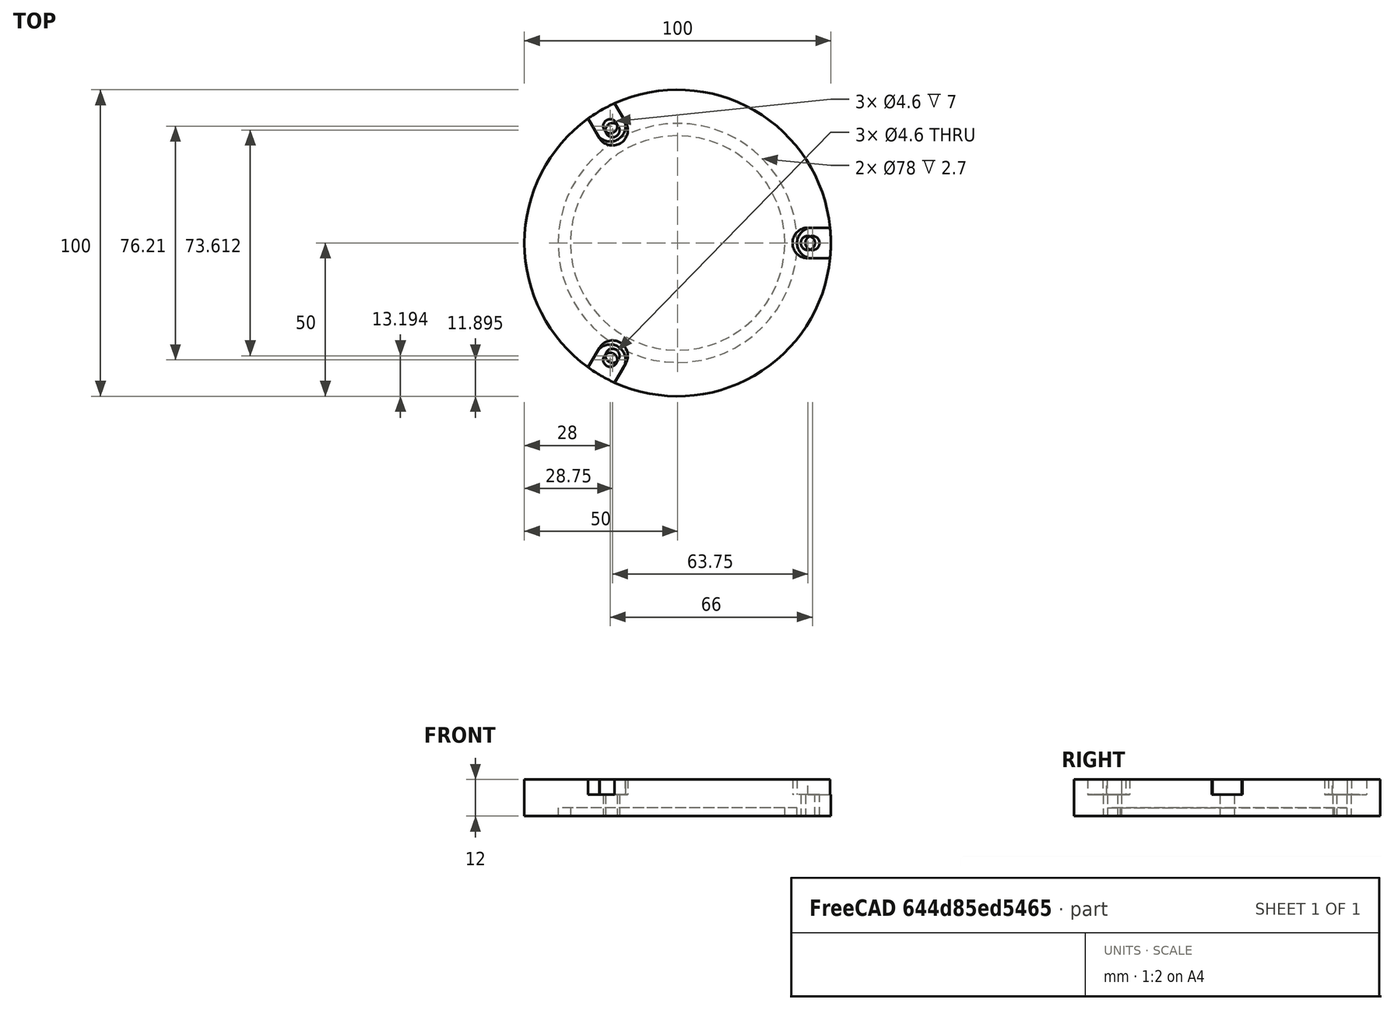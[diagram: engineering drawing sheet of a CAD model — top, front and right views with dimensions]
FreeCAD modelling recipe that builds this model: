
FCSTD DOCUMENT  (FreeCAD 0.20R29603 (Git))
Label: PhilippsXL30_Blindflange_100
License: All rights reserved
LicenseURL: http://en.wikipedia.org/wiki/All_rights_reserved
objects: TechDraw::DrawViewDimension×18, Part::Cylinder×9, Part::MultiFuse×4, TechDraw::DrawProjGroupItem×4, Part::Box×3, Part::Cut×2, Part::Feature×2, TechDraw::DrawSVGTemplate×2, TechDraw::DrawProjGroup×2, TechDraw::DrawPage×2, Part::Compound×1, TechDraw::DrawViewSection×1
note: 21 computed .brp shape members not serialized (recipe doc carries the construction recipe); baked Part::Feature solids carry a one-line shape summary decoded from their .brp

FEATURE [Part::Cylinder] Cylinder  label="Zylinder"
  Angle = 360
  AttacherType = Attacher::AttachEngine3D
  FirstAngle = 0
  Height = 12
  Radius = 50
  SecondAngle = 0
FEATURE [Part::Cylinder] Cylinder001  label="Zylinder001"
  Angle = 360
  AttacherType = Attacher::AttachEngine3D
  FirstAngle = 0
  Height = 2.7
  Radius = 39
  SecondAngle = 0
FEATURE [Part::Cut] Cut
  Base = -> Cylinder
  Tool = -> Cylinder001
FEATURE [Part::Cylinder] Cylinder002  label="Zylinder002"
  Angle = 360
  AttacherType = Attacher::AttachEngine3D
  FirstAngle = 0
  Height = 2.7
  Radius = 35
  SecondAngle = 0
FEATURE [Part::MultiFuse] Fusion
  Shapes = -> [Cylinder002,Cut]
FEATURE [Part::Cylinder] Cylinder003  label="Zylinder003"
  Angle = 360
  AttacherType = Attacher::AttachEngine3D
  FirstAngle = 0
  Height = 12
  Placement = pos=(44,0,0) rot=(0,0,1;0rad)
  Radius = 2.3
  SecondAngle = 0
FEATURE [Part::Cylinder] Cylinder004  label="Zylinder004"
  Angle = 360
  AttacherType = Attacher::AttachEngine3D
  FirstAngle = 0
  Height = 5
  Placement = pos=(44,0,7) rot=(0,0,1;0rad)
  Radius = 5
  SecondAngle = 0
FEATURE [Part::Box] Box  label="Würfel"
  AttacherType = Attacher::AttachEngine3D
  Height = 5
  Length = 10
  Placement = pos=(42.5,-5,7) rot=(0,0,1;0rad)
  Width = 10
FEATURE [Part::MultiFuse] Fusion001
  Shapes = -> [Box,Cylinder003,Cylinder004]
FEATURE [Part::Box] Box001  label="Würfel001"
  AttacherType = Attacher::AttachEngine3D
  Height = 5
  Length = 10
  Placement = pos=(42.5,-5,7) rot=(0,0,1;0rad)
  Width = 10
FEATURE [Part::Cylinder] Cylinder005  label="Zylinder005"
  Angle = 360
  AttacherType = Attacher::AttachEngine3D
  FirstAngle = 0
  Height = 12
  Placement = pos=(44,0,0) rot=(0,0,1;0rad)
  Radius = 2.3
  SecondAngle = 0
FEATURE [Part::Cylinder] Cylinder006  label="Zylinder006"
  Angle = 360
  AttacherType = Attacher::AttachEngine3D
  FirstAngle = 0
  Height = 5
  Placement = pos=(44,0,7) rot=(0,0,1;0rad)
  Radius = 5
  SecondAngle = 0
FEATURE [Part::MultiFuse] Fusion002
  Placement = pos=(0,0,0) rot=(0,0,1;2.0944rad)
  Shapes = -> [Box001,Cylinder005,Cylinder006]
FEATURE [Part::Box] Box002  label="Würfel002"
  AttacherType = Attacher::AttachEngine3D
  Height = 5
  Length = 10
  Placement = pos=(42.5,-5,7) rot=(0,0,1;0rad)
  Width = 10
FEATURE [Part::Cylinder] Cylinder007  label="Zylinder007"
  Angle = 360
  AttacherType = Attacher::AttachEngine3D
  FirstAngle = 0
  Height = 12
  Placement = pos=(44,0,0) rot=(0,0,1;0rad)
  Radius = 2.3
  SecondAngle = 0
FEATURE [Part::Cylinder] Cylinder008  label="Zylinder008"
  Angle = 360
  AttacherType = Attacher::AttachEngine3D
  FirstAngle = 0
  Height = 5
  Placement = pos=(44,0,7) rot=(0,0,1;0rad)
  Radius = 5
  SecondAngle = 0
FEATURE [Part::MultiFuse] Fusion003
  Placement = pos=(0,0,0) rot=(0,0,1;4.18879rad)
  Shapes = -> [Box002,Cylinder007,Cylinder008]
FEATURE [Part::Compound] Compound
  Links = -> [Fusion001,Fusion002,Fusion003]
FEATURE [Part::Cut] Cut001
  Base = -> Fusion
  Tool = -> Compound
FEATURE [Part::Feature] Cut001_solid  label="Cut001 (Solid)"
  shape: bbox 100 x 100 x 12 mm, 28 faces (baked)
FEATURE [TechDraw::DrawSVGTemplate] Template
  EditableTexts = Designed_by_Name=Thomas Spielauer; FC-Date=2023-07-05; FC-SC=mm; FC-SH=01/02; FC-Title=Philipps XL 30 blind flange (100); Subtitle=Compatible
  Height = 210
  Orientation = 1
  Width = 297
FEATURE [TechDraw::DrawProjGroupItem] ProjItem  label="Front"
  CoarseView = false
  Direction = (0,0,1)
  Focus = 100
  HardHidden = false
  IsoCount = 0
  IsoHidden = false
  IsoVisible = false
  LockPosition = true
  Perspective = false
  Rotation = 0
  RotationVector = (-1,0,0)
  ScaleType = 2
  SeamHidden = false
  SeamVisible = true
  SmoothHidden = false
  SmoothVisible = true
  Source = -> [Cut001]
  Type = 0
  X = 0
  XDirection = (-1,0,0)
  Y = 0
FEATURE [TechDraw::DrawProjGroupItem] ProjItem001  label="Right"
  CoarseView = false
  Direction = (-1,0,1e-16)
  Focus = 100
  HardHidden = false
  IsoCount = 0
  IsoHidden = false
  IsoVisible = false
  LockPosition = false
  Perspective = false
  Rotation = 0
  RotationVector = (1,0,0)
  ScaleType = 2
  SeamHidden = false
  SeamVisible = true
  SmoothHidden = false
  SmoothVisible = true
  Source = -> [Cut001]
  Type = 2
  X = -115
  XDirection = (-1e-16,0,-1)
  Y = 0
FEATURE [TechDraw::DrawViewDimension] Dimension
  AngleOverride = false
  Arbitrary = false
  ArbitraryTolerances = false
  EqualTolerance = true
  ExtensionAngle = 0
  FormatSpec = %.2w
  FormatSpecOverTolerance = %+.2w
  FormatSpecUnderTolerance = %+.2w
  Inverted = false
  LineAngle = 0
  LockPosition = false
  MeasureType = 1
  OverTolerance = 0
  References2D = -> [ProjItem001]
  Rotation = 0
  ScaleType = 0
  TheoreticalExact = false
  Type = 0
  UnderTolerance = 0
  X = 19.2083
  Y = 59.9207
FEATURE [TechDraw::DrawViewDimension] Dimension001
  AngleOverride = false
  Arbitrary = false
  ArbitraryTolerances = false
  EqualTolerance = true
  ExtensionAngle = 0
  FormatSpec = %.2w
  FormatSpecOverTolerance = %+.2w
  FormatSpecUnderTolerance = %+.2w
  Inverted = false
  LineAngle = 0
  LockPosition = false
  MeasureType = 1
  OverTolerance = 0
  References2D = -> [ProjItem001]
  Rotation = 0
  ScaleType = 0
  TheoreticalExact = false
  Type = 0
  UnderTolerance = 0
  X = -19.7857
  Y = -35.9202
FEATURE [TechDraw::DrawViewDimension] Dimension002
  AngleOverride = false
  Arbitrary = false
  ArbitraryTolerances = false
  EqualTolerance = true
  ExtensionAngle = 0
  FormatSpec = %.2w
  FormatSpecOverTolerance = %+.2w
  FormatSpecUnderTolerance = %+.2w
  Inverted = false
  LineAngle = 0
  LockPosition = false
  MeasureType = 1
  OverTolerance = 0
  References2D = -> [ProjItem001]
  Rotation = 0
  ScaleType = 0
  TheoreticalExact = false
  Type = 0
  UnderTolerance = 0
  X = -13.2618
  Y = 53.2317
FEATURE [TechDraw::DrawViewDimension] Dimension003
  AngleOverride = false
  Arbitrary = false
  ArbitraryTolerances = false
  EqualTolerance = true
  ExtensionAngle = 0
  FormatSpec = %.2w
  FormatSpecOverTolerance = %+.2w
  FormatSpecUnderTolerance = %+.2w
  Inverted = false
  LineAngle = 0
  LockPosition = false
  MeasureType = 1
  OverTolerance = 0
  References2D = -> [ProjItem001]
  Rotation = 0
  ScaleType = 0
  TheoreticalExact = false
  Type = 0
  UnderTolerance = 0
  X = 0.218931
  Y = -64.4994
FEATURE [TechDraw::DrawViewDimension] Dimension004
  AngleOverride = false
  Arbitrary = false
  ArbitraryTolerances = false
  EqualTolerance = true
  ExtensionAngle = 0
  FormatSpec = R%.2w
  FormatSpecOverTolerance = %+.2w
  FormatSpecUnderTolerance = %+.2w
  Inverted = false
  LineAngle = 0
  LockPosition = false
  MeasureType = 1
  OverTolerance = 0
  References2D = -> [ProjItem]
  Rotation = 0
  ScaleType = 0
  TheoreticalExact = false
  Type = 4
  UnderTolerance = 0
  X = -6.18987
  Y = 19.3502
FEATURE [TechDraw::DrawViewDimension] Dimension005
  AngleOverride = false
  Arbitrary = false
  ArbitraryTolerances = false
  EqualTolerance = true
  ExtensionAngle = 0
  FormatSpec = ⌀%.2w (3x)
  FormatSpecOverTolerance = %+.2w
  FormatSpecUnderTolerance = %+.2w
  Inverted = false
  LineAngle = 0
  LockPosition = false
  MeasureType = 1
  OverTolerance = 0
  References2D = -> [ProjItem]
  Rotation = 0
  ScaleType = 0
  TheoreticalExact = false
  Type = 5
  UnderTolerance = 0
  X = -25.1053
  Y = -2.37354
FEATURE [TechDraw::DrawViewDimension] Dimension006
  AngleOverride = false
  Arbitrary = false
  ArbitraryTolerances = false
  EqualTolerance = true
  ExtensionAngle = 0
  FormatSpec = ⌀%.2w (3x)
  FormatSpecOverTolerance = %+.2w
  FormatSpecUnderTolerance = %+.2w
  Inverted = false
  LineAngle = 0
  LockPosition = false
  MeasureType = 1
  OverTolerance = 0
  References2D = -> [ProjItem]
  Rotation = 0
  ScaleType = 0
  TheoreticalExact = false
  Type = 5
  UnderTolerance = 0
  X = 28.0562
  Y = -19.9323
FEATURE [TechDraw::DrawProjGroupItem] ProjItem002  label="Rear"
  CoarseView = false
  Direction = (0,0,-1)
  Focus = 100
  HardHidden = false
  IsoCount = 0
  IsoHidden = false
  IsoVisible = false
  LockPosition = false
  Perspective = false
  Rotation = 0
  RotationVector = (1,0,0)
  ScaleType = 2
  SeamHidden = false
  SeamVisible = true
  SmoothHidden = false
  SmoothVisible = true
  Source = -> [Cut001]
  Type = 3
  X = 115
  XDirection = (1,0,0)
  Y = 0
FEATURE [TechDraw::DrawProjGroup] ProjGroup
  Anchor = -> ProjItem
  AutoDistribute = true
  LockPosition = false
  ProjectionType = 0
  Rotation = 0
  ScaleType = 0
  Source = -> [Cut001]
  Views = -> [ProjItem,ProjItem001,ProjItem002]
  X = 116.126
  Y = 130.742
  spacingX = 15
  spacingY = 15
FEATURE [TechDraw::DrawViewDimension] Dimension007
  AngleOverride = false
  Arbitrary = false
  ArbitraryTolerances = false
  EqualTolerance = true
  ExtensionAngle = 0
  FormatSpec = ⌀%.2w
  FormatSpecOverTolerance = %+.2w
  FormatSpecUnderTolerance = %+.2w
  Inverted = false
  LineAngle = 0
  LockPosition = false
  MeasureType = 1
  OverTolerance = 0
  References2D = -> [ProjItem002]
  Rotation = 0
  ScaleType = 0
  TheoreticalExact = false
  Type = 5
  UnderTolerance = 0
  X = 42.307
  Y = -41.3708
FEATURE [TechDraw::DrawViewDimension] Dimension008
  AngleOverride = false
  Arbitrary = false
  ArbitraryTolerances = false
  EqualTolerance = true
  ExtensionAngle = 0
  FormatSpec = ⌀%.2w
  FormatSpecOverTolerance = %+.2w
  FormatSpecUnderTolerance = %+.2w
  Inverted = false
  LineAngle = 0
  LockPosition = false
  MeasureType = 1
  OverTolerance = 0
  References2D = -> [ProjItem002]
  Rotation = 0
  ScaleType = 0
  TheoreticalExact = false
  Type = 5
  UnderTolerance = 0
  X = 34.8456
  Y = -46.8908
FEATURE [TechDraw::DrawViewDimension] Dimension009
  AngleOverride = false
  Arbitrary = false
  ArbitraryTolerances = false
  EqualTolerance = true
  ExtensionAngle = 0
  FormatSpec = ⌀%.2w
  FormatSpecOverTolerance = %+.2w
  FormatSpecUnderTolerance = %+.2w
  Inverted = false
  LineAngle = 0
  LockPosition = false
  MeasureType = 1
  OverTolerance = 0
  References2D = -> [ProjItem002]
  Rotation = 0
  ScaleType = 0
  TheoreticalExact = false
  Type = 5
  UnderTolerance = 0
  X = 27.1227
  Y = -51.2481
FEATURE [TechDraw::DrawViewDimension] Dimension010
  AngleOverride = false
  Arbitrary = false
  ArbitraryTolerances = false
  EqualTolerance = true
  ExtensionAngle = 0
  FormatSpec = %.2w
  FormatSpecOverTolerance = %+.2w
  FormatSpecUnderTolerance = %+.2w
  Inverted = false
  LineAngle = 0
  LockPosition = false
  MeasureType = 1
  OverTolerance = 0
  References2D = -> [ProjItem]
  Rotation = 0
  ScaleType = 0
  TheoreticalExact = false
  Type = 6
  UnderTolerance = 0
  X = 25.5814
  Y = 14.9594
FEATURE [TechDraw::DrawPage] Page
  KeepUpdated = true
  NextBalloonIndex = 1
  ProjectionType = 0
  Template = -> Template
  Views = -> [ProjGroup,Dimension,Dimension001,Dimension002,Dimension003,Dimension004,Dimension005,Dimension006,Dimension007,Dimension008,Dimension009,Dimension010]
FEATURE [TechDraw::DrawSVGTemplate] Template001
  EditableTexts = Designed_by_Name=Thomas Spielauer; FC-Date=2023-07-05; FC-SC=mm; FC-SH=02/02; FC-Title=Philipps XL 30 blind flange (100); Subtitle=Compatible
  Height = 210
  Orientation = 1
  Width = 297
FEATURE [TechDraw::DrawProjGroupItem] ProjItem003  label="Front001"
  CoarseView = false
  Direction = (0,0,1)
  Focus = 100
  HardHidden = false
  IsoCount = 0
  IsoHidden = false
  IsoVisible = false
  LockPosition = true
  Perspective = false
  Rotation = 0
  RotationVector = (-1,0,0)
  ScaleType = 2
  SeamHidden = false
  SeamVisible = true
  SmoothHidden = false
  SmoothVisible = true
  Source = -> [Cut001]
  Type = 0
  X = 0
  XDirection = (-1e-16,-1,0)
  Y = 0
FEATURE [TechDraw::DrawProjGroup] ProjGroup001
  Anchor = -> ProjItem003
  AutoDistribute = true
  LockPosition = false
  ProjectionType = 0
  Rotation = 0
  ScaleType = 0
  Source = -> [Cut001]
  Views = -> [ProjItem003]
  X = 83.2538
  Y = 132.097
  spacingX = 15
  spacingY = 15
FEATURE [TechDraw::DrawViewSection] SectionView  label="Section  - "
  BaseView = -> ProjItem003
  CoarseView = false
  CutSurfaceDisplay = 2
  Direction = (1e-16,1,0)
  FileGeomPattern = <path>
  FileHatchPattern = <path>
  Focus = 100
  FuseBeforeCut = false
  HardHidden = false
  HatchScale = 1
  IsoCount = 0
  IsoHidden = false
  IsoVisible = false
  LockPosition = false
  NameGeomPattern = Diamond
  Perspective = false
  Rotation = 0
  ScaleType = 2
  SeamHidden = false
  SeamVisible = true
  SectionDirection = 0
  SectionNormal = (1e-16,1,0)
  SectionOrigin = (0,0,6)
  SmoothHidden = false
  SmoothVisible = true
  Source = -> [Cut001]
  X = 195.097
  XDirection = (0,0,1)
  Y = 133.77
FEATURE [TechDraw::DrawViewDimension] Dimension011
  AngleOverride = false
  Arbitrary = false
  ArbitraryTolerances = false
  EqualTolerance = true
  ExtensionAngle = 0
  FormatSpec = %.2w
  FormatSpecOverTolerance = %+.2w
  FormatSpecUnderTolerance = %+.2w
  Inverted = false
  LineAngle = 0
  LockPosition = false
  MeasureType = 1
  OverTolerance = 0
  References2D = -> [SectionView]
  Rotation = 0
  ScaleType = 0
  TheoreticalExact = false
  Type = 0
  UnderTolerance = 0
  X = -20.9799
  Y = -22.9677
FEATURE [TechDraw::DrawViewDimension] Dimension012
  AngleOverride = false
  Arbitrary = false
  ArbitraryTolerances = false
  EqualTolerance = true
  ExtensionAngle = 0
  FormatSpec = %.2w
  FormatSpecOverTolerance = %+.2w
  FormatSpecUnderTolerance = %+.2w
  Inverted = false
  LineAngle = 0
  LockPosition = false
  MeasureType = 1
  OverTolerance = 0
  References2D = -> [SectionView]
  Rotation = 0
  ScaleType = 0
  TheoreticalExact = false
  Type = 0
  UnderTolerance = 0
  X = 1.48289
  Y = -56.7363
FEATURE [TechDraw::DrawViewDimension] Dimension013
  AngleOverride = false
  Arbitrary = false
  ArbitraryTolerances = false
  EqualTolerance = true
  ExtensionAngle = 0
  FormatSpec = %.2w
  FormatSpecOverTolerance = %+.2w
  FormatSpecUnderTolerance = %+.2w
  Inverted = false
  LineAngle = 0
  LockPosition = false
  MeasureType = 1
  OverTolerance = 0
  References2D = -> [SectionView]
  Rotation = 0
  ScaleType = 0
  TheoreticalExact = false
  Type = 0
  UnderTolerance = 0
  X = 8.24155
  Y = 57.3473
FEATURE [TechDraw::DrawViewDimension] Dimension014
  AngleOverride = false
  Arbitrary = false
  ArbitraryTolerances = false
  EqualTolerance = true
  ExtensionAngle = 0
  FormatSpec = %.2w
  FormatSpecOverTolerance = %+.2w
  FormatSpecUnderTolerance = %+.2w
  Inverted = false
  LineAngle = 0
  LockPosition = false
  MeasureType = 1
  OverTolerance = 0
  References2D = -> [SectionView]
  Rotation = 0
  ScaleType = 0
  TheoreticalExact = false
  Type = 0
  UnderTolerance = 0
  X = 15.2326
  Y = -64.242
FEATURE [TechDraw::DrawViewDimension] Dimension015
  AngleOverride = false
  Arbitrary = false
  ArbitraryTolerances = false
  EqualTolerance = true
  ExtensionAngle = 0
  FormatSpec = %.2w
  FormatSpecOverTolerance = %+.2w
  FormatSpecUnderTolerance = %+.2w
  Inverted = false
  LineAngle = 0
  LockPosition = false
  MeasureType = 1
  OverTolerance = 0
  References2D = -> [SectionView]
  Rotation = 0
  ScaleType = 0
  TheoreticalExact = false
  Type = 0
  UnderTolerance = 0
  X = -44.5438
  Y = 57.2435
FEATURE [TechDraw::DrawViewDimension] Dimension016
  AngleOverride = false
  Arbitrary = false
  ArbitraryTolerances = false
  EqualTolerance = true
  ExtensionAngle = 0
  FormatSpec = %.2w
  FormatSpecOverTolerance = %+.2w
  FormatSpecUnderTolerance = %+.2w
  Inverted = false
  LineAngle = 0
  LockPosition = false
  MeasureType = 1
  OverTolerance = 0
  References2D = -> [SectionView]
  Rotation = 0
  ScaleType = 0
  TheoreticalExact = false
  Type = 0
  UnderTolerance = 0
  X = -36.5591
  Y = 57.7691
FEATURE [TechDraw::DrawViewDimension] Dimension017
  AngleOverride = false
  Arbitrary = false
  ArbitraryTolerances = false
  EqualTolerance = true
  ExtensionAngle = 0
  FormatSpec = %.2w
  FormatSpecOverTolerance = %+.2w
  FormatSpecUnderTolerance = %+.2w
  Inverted = false
  LineAngle = 0
  LockPosition = false
  MeasureType = 1
  OverTolerance = 0
  References2D = -> [SectionView]
  Rotation = 0
  ScaleType = 0
  TheoreticalExact = false
  Type = 0
  UnderTolerance = 0
  X = 25.1073
  Y = 46.7743
FEATURE [TechDraw::DrawPage] Page001
  KeepUpdated = true
  NextBalloonIndex = 1
  ProjectionType = 0
  Template = -> Template001
  Views = -> [ProjGroup001,SectionView,Dimension011,Dimension012,Dimension013,Dimension014,Dimension015,Dimension016,Dimension017]
FEATURE [Part::Feature] Cut001_solid001  label="Cut001 (Solid)v2"
  shape: bbox 100 x 100 x 12 mm, 46 faces (baked)
note: 2 file-system paths scrubbed to <path> (originals preserved in the JSON sidecar)
